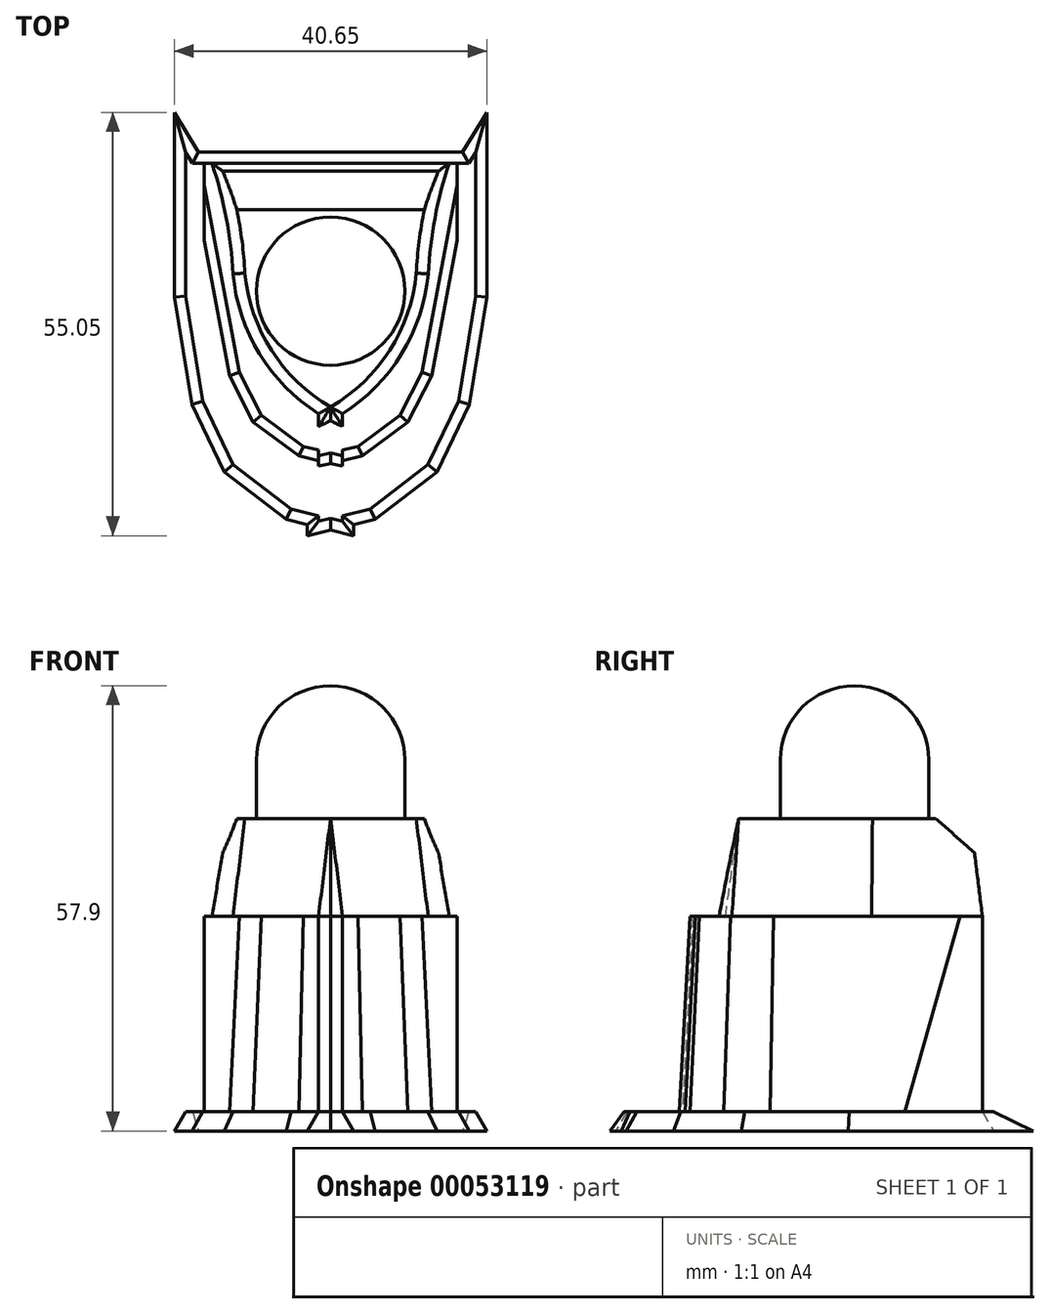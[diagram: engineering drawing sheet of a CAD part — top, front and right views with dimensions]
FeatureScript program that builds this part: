
annotation { "Feature Type Name" : "Feature", "Feature Type Description" : "" }
export const myFeature = defineFeature(function(context is Context, id is Id, definition is map)
    precondition{}
    {
        {
            var Q0;
            Q0=qCreatedBy(makeId("Top.planeOp"),FACE);
            var sketch = newSketch(context, id + "F0", { "sketchPlane" : qUnion([Q0])});
            skLineSegment(sketch, "E0", {"start": v(0, -55.05) * mm, "end": v(8.8, -52.93) * mm});
            skLineSegment(sketch, "E1", {"start": v(8.8, -52.93) * mm, "end": v(16.87, -46.76) * mm});
            skLineSegment(sketch, "E2", {"start": v(16.87, -46.76) * mm, "end": v(21.08, -37.98) * mm});
            skLineSegment(sketch, "E3", {"start": v(21.08, -37.98) * mm, "end": v(23.35, -24.03) * mm});
            skLineSegment(sketch, "E4", {"start": v(23.35, -24.03) * mm, "end": v(23.35, -10.3) * mm});
            skLineSegment(sketch, "E5", {"start": v(23.35, -10.3) * mm, "end": v(23.35, 0) * mm});
            skLineSegment(sketch, "E6", {"start": v(23.35, 0) * mm, "end": v(20.2, -5.15) * mm});
            skPoint(sketch, "E6.endSnap0", {"position": v(23.35, -5.15) * mm});
            skLineSegment(sketch, "E7", {"start": v(20.2, -5.15) * mm, "end": v(0, -5.15) * mm});
            skLineSegment(sketch, "E8", {"start": v(0, -5.15) * mm, "end": v(0, -55.05) * mm});
            skSolve(sketch);
        }
        {
            var Q0;
            Q0 = qSketchRegion(id + "F0", true);
            extrude(context, id + "F1", {"entities" : qUnion([Q0]), "depth" : 2.54 * mm, "hasDraft" : true, "draftAngle" : 30 * degree, "draftPullDirection" : true});
        }
        {
            var Q0;
            Q0=makeQuery(id+"F1.opExtrude","CAP_FACE",FACE,{"disambiguationData":[OSD([sQuery(id+"F0.wireOp",EDGE,"E0"),sQuery(id+"F0.wireOp",EDGE,"E1"),sQuery(id+"F0.wireOp",EDGE,"E2"),sQuery(id+"F0.wireOp",EDGE,"E3"),sQuery(id+"F0.wireOp",EDGE,"E4"),sQuery(id+"F0.wireOp",EDGE,"E5"),sQuery(id+"F0.wireOp",EDGE,"E6"),sQuery(id+"F0.wireOp",EDGE,"E7"),sQuery(id+"F0.wireOp",EDGE,"E8")])],"isStart":false});
            var sketch = newSketch(context, id + "F2", { "sketchPlane" : qUnion([Q0])});
            skLineSegment(sketch, "E9", {"start": v(19.48, -6.62) * mm, "end": v(19.48, -23.88) * mm});
            skLineSegment(sketch, "E10", {"start": v(19.48, -23.88) * mm, "end": v(17.45, -34.65) * mm});
            skLineSegment(sketch, "E11", {"start": v(17.45, -34.65) * mm, "end": v(14.14, -41.15) * mm});
            skLineSegment(sketch, "E12", {"start": v(14.14, -41.15) * mm, "end": v(7.73, -45.89) * mm});
            skLineSegment(sketch, "E13", {"start": v(7.73, -45.89) * mm, "end": v(1.47, -47.38) * mm});
            skLineSegment(sketch, "E14", {"start": v(1.47, -47.38) * mm, "end": v(1.47, -6.62) * mm});
            skLineSegment(sketch, "E15", {"start": v(1.47, -6.62) * mm, "end": v(19.48, -6.62) * mm});
            skSolve(sketch);
        }
        {
            var Q0;
            Q0 = qSketchRegion(id + "F2", true);
            extrude(context, id + "F3", {"entities" : qUnion([Q0]), "operationType" : NewBodyOperationType.ADD, "depth" : 25.4 * mm});
        }
        {
            var Q0;
            Q0=makeQuery(id+"F3.opExtrude","CAP_EDGE",EDGE,{"disambiguationData":[OSD([sQuery(id+"F2.wireOp",EDGE,"E13")])],"isStart":false});
            chamfer(context, id + "F4", {"entities" : qUnion([Q0]), "chamferType" : ChamferType.OFFSET_ANGLE, "width" : 50.8 * mm, "oppositeDirection" : false, "angle" : 3 * degree, "tangentPropagation" : true});
        }
        {
            var Q0;
            Q0=makeQuery(id+"F3.opExtrude","CAP_EDGE",EDGE,{"disambiguationData":[OSD([sQuery(id+"F2.wireOp",EDGE,"E12")])],"isStart":false});
            chamfer(context, id + "F5", {"entities" : qUnion([Q0]), "chamferType" : ChamferType.OFFSET_ANGLE, "width" : 50.8 * mm, "oppositeDirection" : false, "angle" : 3 * degree, "tangentPropagation" : true});
        }
        {
            var Q0;
            Q0=makeQuery(id+"F3.opExtrude","CAP_EDGE",EDGE,{"disambiguationData":[OSD([sQuery(id+"F2.wireOp",EDGE,"E11")])],"isStart":false});
            chamfer(context, id + "F6", {"entities" : qUnion([Q0]), "chamferType" : ChamferType.OFFSET_ANGLE, "width" : 50.8 * mm, "oppositeDirection" : false, "angle" : 3 * degree, "tangentPropagation" : true});
        }
        {
            var Q0;
            Q0=makeQuery(id+"F3.opExtrude","CAP_EDGE",EDGE,{"disambiguationData":[OSD([sQuery(id+"F2.wireOp",EDGE,"E10")])],"isStart":false});
            chamfer(context, id + "F7", {"entities" : qUnion([Q0]), "chamferType" : ChamferType.OFFSET_ANGLE, "width" : 50.8 * mm, "oppositeDirection" : false, "angle" : 3 * degree, "tangentPropagation" : true});
        }
        {
            var Q0;
            Q0=makeQuery(id+"F3.opExtrude","CAP_FACE",FACE,{"disambiguationData":[OSD([sQuery(id+"F2.wireOp",EDGE,"E9"),sQuery(id+"F2.wireOp",EDGE,"E10"),sQuery(id+"F2.wireOp",EDGE,"E11"),sQuery(id+"F2.wireOp",EDGE,"E12"),sQuery(id+"F2.wireOp",EDGE,"E13"),sQuery(id+"F2.wireOp",EDGE,"E14"),sQuery(id+"F2.wireOp",EDGE,"E15")])],"isStart":false});
            var sketch = newSketch(context, id + "F8", { "sketchPlane" : qUnion([Q0])});
            skArc(sketch, "E16", {"start": v(1.47, -40.83) * mm, "mid": v(11.3, -32.86) * mm, "end": v(15.72, -21) * mm});
            skArc(sketch, "E17", {"start": v(18.44, -6.62) * mm, "mid": v(16.6, -13.72) * mm, "end": v(15.72, -21) * mm});
            skLineSegment(sketch, "E18", {"start": v(1.47, -40.83) * mm, "end": v(1.47, -6.62) * mm});
            skLineSegment(sketch, "E19", {"start": v(1.47, -6.62) * mm, "end": v(18.44, -6.62) * mm});
            skSolve(sketch);
        }
        {
            var Q0;
            Q0 = qSketchRegion(id + "F8", true);
            extrude(context, id + "F9", {"entities" : qUnion([Q0]), "operationType" : NewBodyOperationType.ADD, "depth" : 12.7 * mm, "hasDraft" : true, "draftAngle" : 7 * degree, "draftPullDirection" : true});
        }
        {
            var Q0;
            Q0=makeQuery(id+"F9.opExtrude","CAP_FACE",FACE,{"disambiguationData":[OSD([sQuery(id+"F8.wireOp",EDGE,"E16"),sQuery(id+"F8.wireOp",EDGE,"E17"),sQuery(id+"F8.wireOp",EDGE,"E18"),sQuery(id+"F8.wireOp",EDGE,"E19")])],"isStart":false});
            var sketch = newSketch(context, id + "F10", { "sketchPlane" : qUnion([Q0])});
            skArc(sketch, "E20", {"start": v(3.03, -32.88) * mm, "mid": v(12.67, -23.24) * mm, "end": v(3.03, -13.6) * mm});
            skSolve(sketch);
        }
        {
            var Q0;
            {var subQ0=sQuery(id+"F10.wireOp",EDGE,"E20");Q0=makeQuery(id+"F10.imprint","IMPRINT",FACE,{"disambiguationData":[TD([[makeQuery(id+"F10.imprint","IMPRINT",EDGE,{"derivedFrom":subQ0}),1.0]])]});}
            extrude(context, id + "F11", {"entities" : qUnion([Q0]), "operationType" : NewBodyOperationType.ADD, "depth" : 7.62 * mm});
        }
        {
            var Q0;
            Q0=makeQuery(id+"F11.opExtrude","CAP_FACE",FACE,{"disambiguationData":[OSD([sQuery(id+"F8.wireOp",EDGE,"E18"),sQuery(id+"F10.wireOp",EDGE,"E20")])],"isStart":false});
            var Q1;
            Q1=makeQuery(id+"F11.opExtrude","CAP_EDGE",EDGE,{"disambiguationData":[OSD([sQuery(id+"F8.wireOp",EDGE,"E18")])],"isStart":false});
            revolve(context, id + "F12", {"operationType" : NewBodyOperationType.ADD, "entities" : qUnion([Q0]), "axis" : qUnion([Q1]), "revolveType" : RevolveType.ONE_DIRECTION, "oppositeDirection" : true, "angle" : 90 * degree});
        }
        {
            var Q0;
            Q0=makeQuery(id+"F9.opExtrude","CAP_EDGE",EDGE,{"disambiguationData":[OSD([sQuery(id+"F8.wireOp",EDGE,"E19")])],"isStart":false});
            chamfer(context, id + "F13", {"entities" : qUnion([Q0]), "width" : 5.08 * mm, "tangentPropagation" : true});
        }
        {
            var Q0;
            {var subQ0=sQuery(id+"F8.wireOp",EDGE,"E18");Q0=makeQuery(id+"F12.boolean.opBoolean","MERGE",FACE,{"derivedFrom":[makeQuery(id+"F11.opExtrude","SWEPT_FACE",FACE,{"disambiguationData":[OSD([subQ0])]}),makeQuery(id+"F12.opRevolve","CAP_FACE",FACE,{"disambiguationData":[OSD([subQ0,sQuery(id+"F10.wireOp",EDGE,"E20")])],"isStart":false})]});}
            cPlane(context, id + "F14", {"entities" : qUnion([Q0]), "cplaneType" : CPlaneType.OFFSET, "offset" : 0 * mm, "width" : 152.4 * mm, "height" : 152.4 * mm});
        }
        {
            var Q0;
            Q0=makeQuery(id+"F1.opExtrude","SWEPT_BODY",BODY,{"disambiguationData":[OSD([sQuery(id+"F0.wireOp",EDGE,"E0"),sQuery(id+"F0.wireOp",EDGE,"E1"),sQuery(id+"F0.wireOp",EDGE,"E2"),sQuery(id+"F0.wireOp",EDGE,"E3"),sQuery(id+"F0.wireOp",EDGE,"E4"),sQuery(id+"F0.wireOp",EDGE,"E5"),sQuery(id+"F0.wireOp",EDGE,"E6"),sQuery(id+"F0.wireOp",EDGE,"E7"),sQuery(id+"F0.wireOp",EDGE,"E8")])]});
            var Q1;
            Q1=qCreatedBy(id+"F14.planeOp",FACE);
            mirror(context, id + "F15", {"operationType" : NewBodyOperationType.ADD, "entities" : qUnion([Q0]), "mirrorPlane" : qUnion([Q1])});
        }
    });
